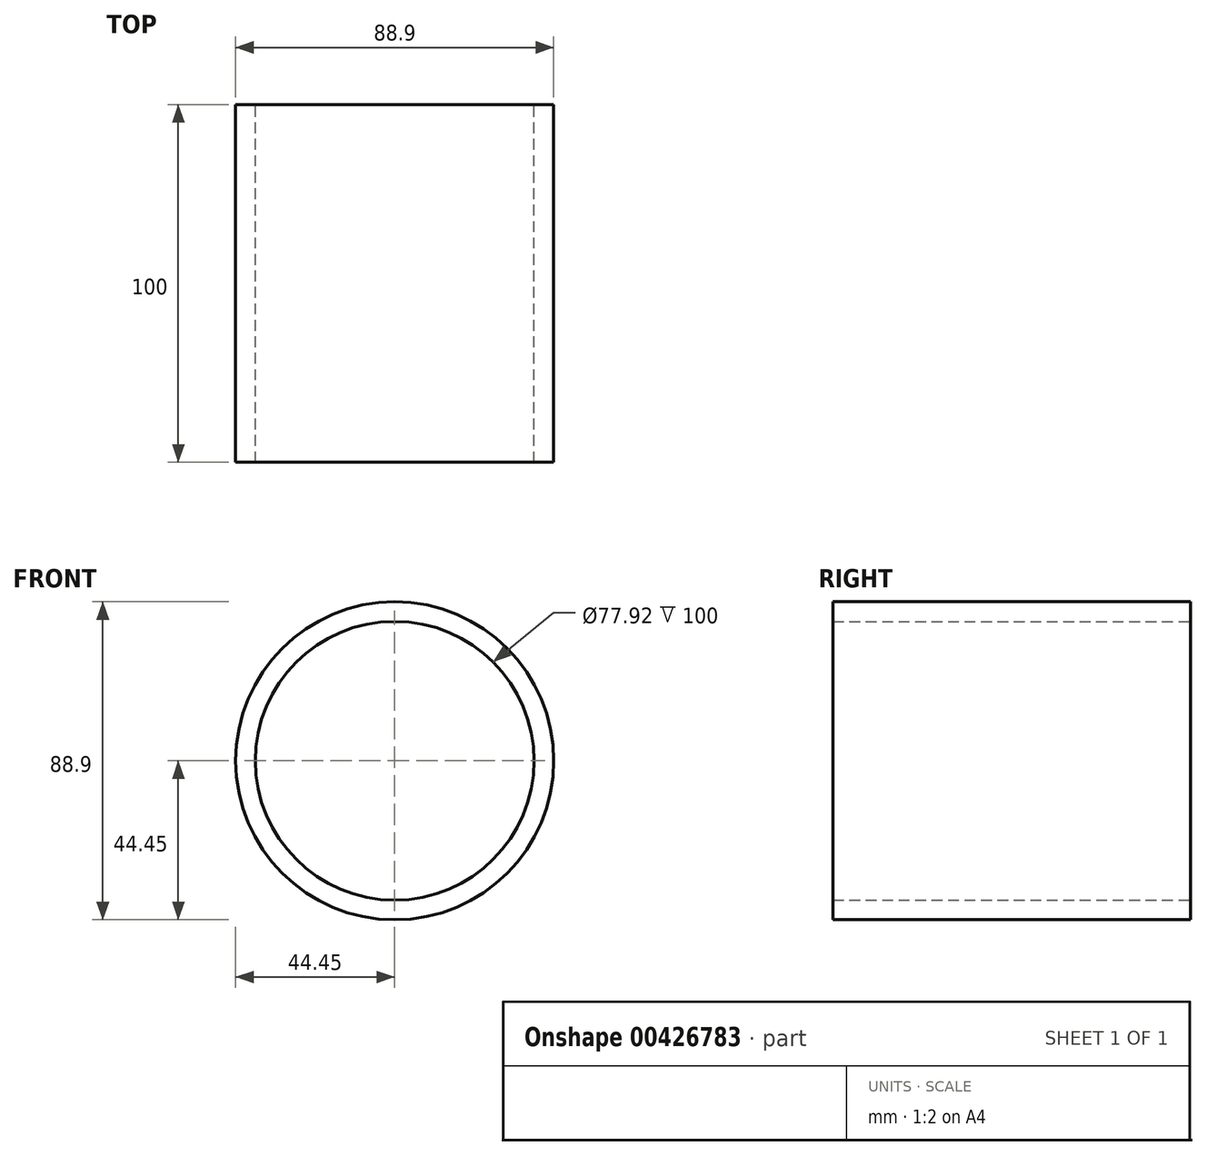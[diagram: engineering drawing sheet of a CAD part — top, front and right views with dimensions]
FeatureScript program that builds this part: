
annotation { "Feature Type Name" : "Feature", "Feature Type Description" : "" }
export const myFeature = defineFeature(function(context is Context, id is Id, definition is map)
    precondition{}
    {
        {
            var Q0;
            Q0=qCreatedBy(makeId("Front.planeOp"),FACE);
            var sketch = newSketch(context, id + "F0", { "sketchPlane" : qUnion([Q0])});
            skCircle(sketch, "E0", {"center": v(0, 0) * mm, "radius": 44.45 * mm});
            skCircle(sketch, "E1.0", {"center": v(0, 0) * mm, "radius": 38.96 * mm});
            skSolve(sketch);
        }
        {
            var Q0;
            Q0=makeQuery(id+"F0.imprint","IMPRINT",FACE,{"disambiguationData":[TD([[makeQuery(id+"F0.imprint","IMPRINT",EDGE,{"derivedFrom":sQuery(id+"F0.wireOp",EDGE,"E0")}),1.0]])]});
            extrude(context, id + "F1", {"entities" : qUnion([Q0]), "depth" : 100 * mm});
        }
    });
